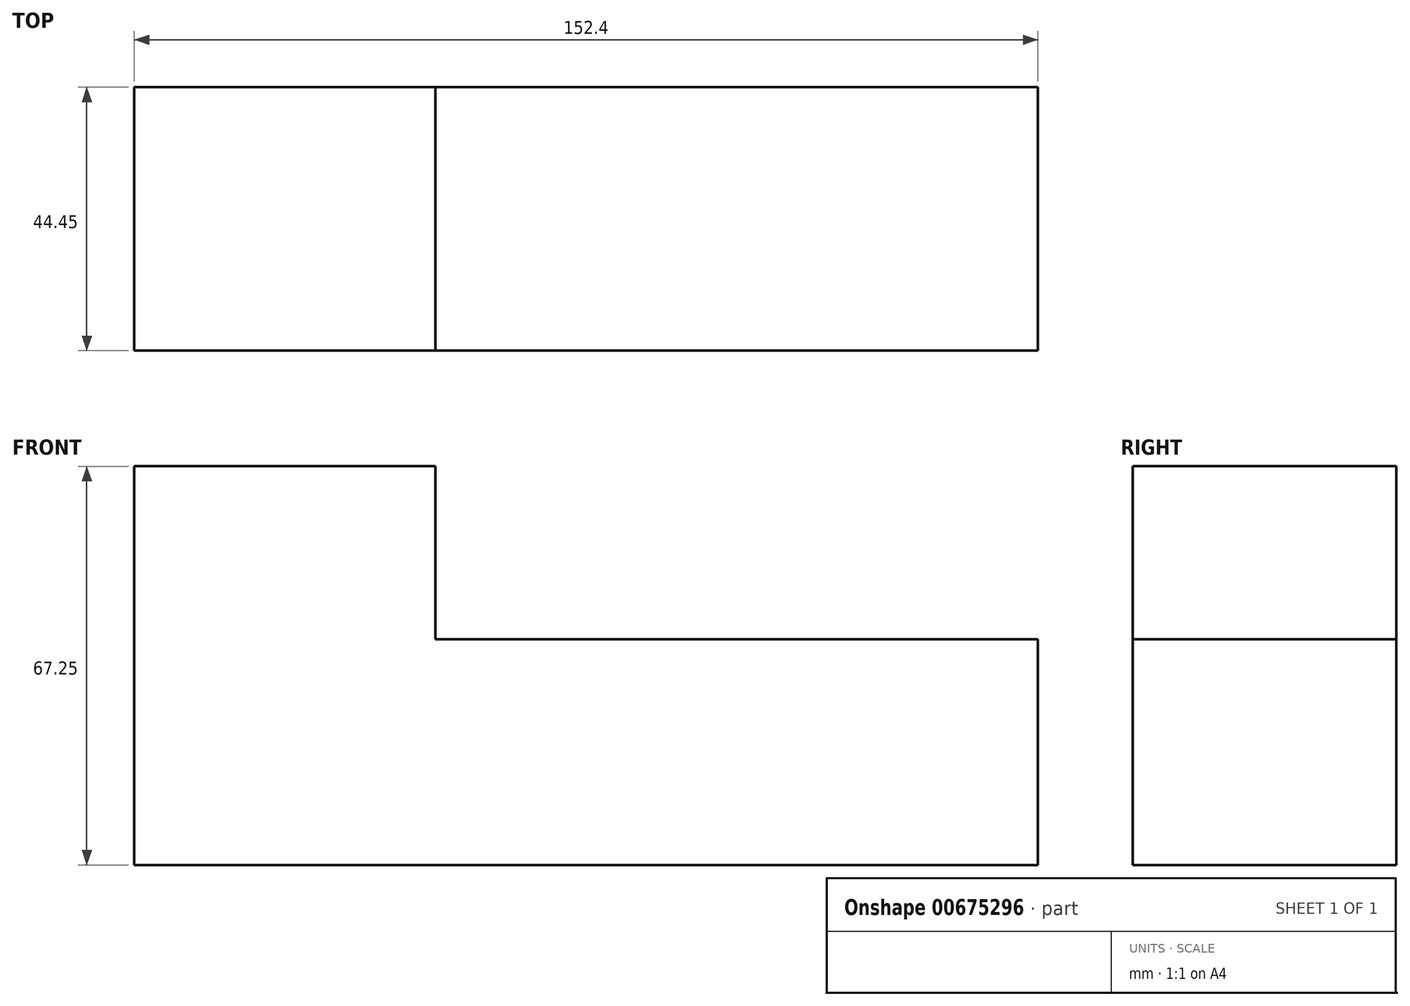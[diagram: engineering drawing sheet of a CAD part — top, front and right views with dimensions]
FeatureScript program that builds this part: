
annotation { "Feature Type Name" : "Feature", "Feature Type Description" : "" }
export const myFeature = defineFeature(function(context is Context, id is Id, definition is map)
    precondition{}
    {
        {
            var Q0;
            Q0=qCreatedBy(makeId("Front.planeOp"),FACE);
            var sketch = newSketch(context, id + "F0", { "sketchPlane" : qUnion([Q0])});
            skLineSegment(sketch, "E0", {"start": v(-41.3, 27.68) * mm, "end": v(-41.3, -39.57) * mm});
            skLineSegment(sketch, "E1", {"start": v(-41.3, -39.57) * mm, "end": v(111.1, -39.57) * mm});
            skLineSegment(sketch, "E2", {"start": v(111.1, -39.57) * mm, "end": v(111.1, -1.47) * mm});
            skLineSegment(sketch, "E3", {"start": v(111.1, -1.47) * mm, "end": v(9.5, -1.47) * mm});
            skLineSegment(sketch, "E4", {"start": v(9.5, -1.47) * mm, "end": v(9.5, 27.68) * mm});
            skLineSegment(sketch, "E5", {"start": v(9.5, 27.68) * mm, "end": v(-41.3, 27.68) * mm});
            skSolve(sketch);
        }
        {
            var Q0;
            Q0=makeQuery(id+"F0.imprint","IMPRINT",FACE,{"disambiguationData":[TD([[makeQuery(id+"F0.imprint","IMPRINT",EDGE,{"derivedFrom":sQuery(id+"F0.wireOp",EDGE,"E0")}),1.0]])]});
            extrude(context, id + "F1", {"entities" : qUnion([Q0]), "depth" : 44.45 * mm, "offsetDistance" : 25.4 * mm});
        }
    });
